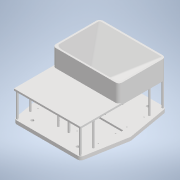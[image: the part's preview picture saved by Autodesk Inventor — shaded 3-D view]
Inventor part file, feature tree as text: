
AUTODESK INVENTOR PART (.ipt)
format: ipt  version: 2021 (Build 250183000, 183)  size: 367,104 bytes
history: native  units: mm
features: reference x19, other x9, extrude x8, sketch x7, plane x2, fillet x1, pattern_linear x1, projected_geometry x1
ambient origin geometry x8: Origin, YZ Plane, XZ Plane, XY Plane, X Axis, Y Axis, Z Axis, Center Point
bodies: Solid1 (feature_tree)
feature tree (48):
  extrude  "Extrusion1"  Depth=200.0mm
  sketch  "Sketch2"  dims[d0=130.0mm d1=200.0mm]
  plane  "Work Plane1"
  extrude  "Extrusion5"  Depth=20.0mm
  extrude  "Extrusion6"  Depth=245.0mm
  fillet  "Fillet3"  Radius=245.0mm
  plane  "Work Plane4"
  extrude  "Extrusion14"  Depth=50.0mm
  extrude  "Extrusion15"  Depth=145.0mm
  pattern_linear  "Rectangular Pattern7"  Count1=2  [1 undecoded]
  extrude  "Extrusion16"  Depth=10.0mm TaperAngle=0.0deg
  extrude  "Extrusion17"  Depth=60.0mm
  extrude  "Extrusion18"  Depth=30.0mm
  reference  "Reference1"
  reference  "Reference2"
  reference  "Reference3"
  reference  "Reference4"
  reference  "Reference5"
  reference  "Reference6"
  reference  "Reference7"
  sketch  "Sketch5"  dims[d2=40.0mm d3=20.0mm]
  reference  "Reference17"
  reference  "Reference18"
  reference  "Reference19"
  reference  "Reference20"
  reference  "Reference21"
  reference  "Reference22"
  reference  "Reference23"
  reference  "Reference24"
  sketch  "Sketch6"  dims[d4=20.0mm d6=200.0mm d7=20.0mm d9=130.0mm d12=190.0mm d13=245.0mm]
  sketch  "Sketch15"  dims[d14=50.0mm d15=50.0mm]
  reference  "Reference27"
  reference  "Reference28"
  reference  "Reference29"
  reference  "Reference30"
  sketch  "Sketch16"  dims[d16=90.0deg d17=145.0mm]
  projected_geometry  "Projected Loop8"
  sketch  "Sketch17"  dims[d18=90.0deg]
  sketch  "Sketch18"  dims[d19=8.0mm d20=20.0mm d22=200.0mm d23=20.0mm d25=130.0mm d28=10.0mm d29=0.0mm d31=60.0mm d32=30.0mm d49=0.0mm d50=0.0mm d51=25.0mm d52=25.0mm d53=0.0mm d54=0.0mm d125=13.962634mm d126=10.0mm d127=10.0mm d128=0.0mm d129=15.0mm d130=0.0mm d134=20.0mm d136=110.0mm d137=190.0mm d138=160.0mm d139=80.0mm d140=175.0mm d141=80.0mm d142=10.0mm d143=10.0mm d144=10.0mm d145=10.0mm d146=10.0mm d147=10.0mm d148=10.0mm d149=10.0mm d150=30.0mm d151=0.0mm d152=100.0mm d153=175.0mm d154=100.0mm d155=175.0mm d156=3.0mm d157=0.0mm d158=180.0mm d159=230.0mm d160=10.0mm d161=10.0mm d162=10.0mm d163=10.0mm d164=0.0mm d165=0.0mm d33=0.5mm d34=0.872665mm d35=0.5mm d36=0.872665mm d62=0.5mm d63=0.872665mm d64=0.5mm d65=0.872665mm]
  parser-record x1  (decoder bookkeeping rows leaked as tree rows — omitted from the tree; the rows remain in map.json)
  other  "ilmbt_3d_v1.iam"
  other  "MG-958 servo_MIR:1"
  other  "Part13_MIR:1"
  other  "motor driver:1"
  other  "motor driver:4"
  other  "motor driver:3"
  other  "motor driver:2"
  other  "MG-958 servo_MIR:5"
note: 1 required parameter value undecoded (feature->parameter linkage not recoverable at this tier; creation-order binding heuristic only, values carry confidence <= 0.55)
note: 1 file-system path scrubbed to <path> (originals preserved in map.json)
